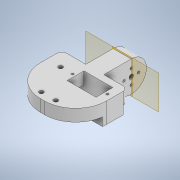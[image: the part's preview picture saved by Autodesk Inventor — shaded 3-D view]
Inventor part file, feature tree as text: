
AUTODESK INVENTOR PART (.ipt)
format: ipt  version: 2021 (Build 250183000, 183)  size: 241,664 bytes
history: native  units: mm
features: sketch x13, extrude x11, fillet x3, plane x2
ambient origin geometry x8: Origin, YZ Plane, XZ Plane, XY Plane, X Axis, Y Axis, Z Axis, Center Point
bodies: Solid1 (feature_tree)
feature tree (29):
  extrude  "Extrusion1"  Depth=15.0mm TaperAngle=0.0deg
  plane  "Work Plane1"
  plane  "Work Plane2"
  extrude  "Extrusion2"  Depth=12.75mm TaperAngle=0.0deg
  extrude  "Extrusion3"  Depth=10.0mm TaperAngle=0.0deg
  sketch  "Sketch4"  dims[d10=27.5mm d11=27.5mm]
  extrude  "Extrusion4"  Depth=27.5mm
  extrude  "Extrusion5"  Depth=43.5mm
  extrude  "Extrusion6"  Depth=4.0mm
  extrude  "Extrusion7"  Depth=17.0mm
  extrude  "Extrusion8"  Depth=1.5mm
  extrude  "Extrusion9"  Depth=14.0mm
  extrude  "Extrusion10"  Depth=5.5mm
  sketch  "Sketch12"  dims[d32=2.0mm]
  fillet  "Fillet1"  Radius=5.5mm
  fillet  "Fillet2"  Radius=20.0mm
  extrude  "Extrusion11"  Depth=2.5mm
  sketch  "Sketch13"  dims[d33=20.0mm d34=0.0mm d35=10.0mm d36=3.5mm d37=5.0mm d38=21.5mm d39=3.5mm d40=12.0mm d41=3.5mm d42=12.0mm d43=0.0mm d44=3.5mm d45=12.0mm d46=0.0mm d47=2.0mm d48=12.0mm d49=0.0mm d50=6.0mm d51=6.0mm d52=6.0mm d53=6.0mm d54=2.0mm d55=2.0mm d56=2.0mm d57=2.0mm d58=25.75mm d59=4.0mm d60=20.0mm d61=0.0mm d62=11.5mm d63=0.872665mm]
  fillet  "Fillet3"  Radius=2.0mm
  sketch  "Sketch1"  dims[d0=25.5mm d1=15.0mm d2=0.0mm]
  sketch  "Sketch2"  dims[d3=0.0mm d4=0.0mm d5=12.75mm d6=0.0mm]
  sketch  "Sketch3"  dims[d7=10.0mm d8=10.0mm d9=0.0mm]
  sketch  "Sketch5"  dims[d12=55.0mm d13=43.5mm]
  sketch  "Sketch6"  dims[d14=10.0mm d15=0.0mm d16=4.0mm]
  sketch  "Sketch7"  dims[d17=38.0mm d18=17.0mm]
  sketch  "Sketch8"  dims[d19=1.5mm d20=1.5mm]
  sketch  "Sketch9"  dims[d21=35.0mm d22=14.0mm]
  sketch  "Sketch10"  dims[d23=7.0mm d24=0.0mm d25=5.5mm d26=5.5mm d27=20.0mm d28=0.0mm]
  sketch  "Sketch11"  dims[d29=2.5mm d30=2.5mm d31=2.0mm]
